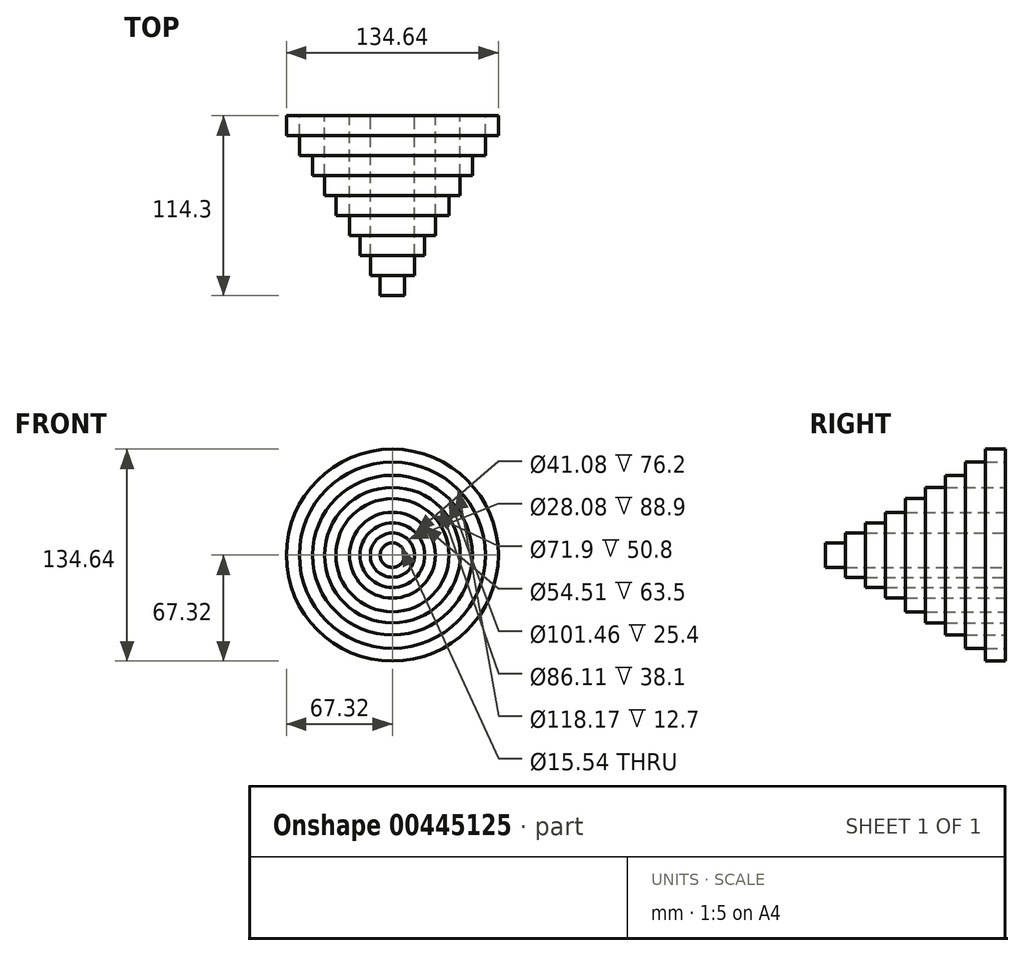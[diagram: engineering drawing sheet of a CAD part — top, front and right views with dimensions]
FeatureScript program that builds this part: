
annotation { "Feature Type Name" : "Feature", "Feature Type Description" : "" }
export const myFeature = defineFeature(function(context is Context, id is Id, definition is map)
    precondition{}
    {
        {
            var Q0;
            Q0=qCreatedBy(makeId("Front.planeOp"),FACE);
            var sketch = newSketch(context, id + "F0", { "sketchPlane" : qUnion([Q0])});
            skCircle(sketch, "E0", {"center": v(0, 0) * mm, "radius": 7.77 * mm});
            skCircle(sketch, "E1", {"center": v(0, 0) * mm, "radius": 14.04 * mm});
            skCircle(sketch, "E2", {"center": v(0, 0) * mm, "radius": 20.54 * mm});
            skCircle(sketch, "E3", {"center": v(0, 0) * mm, "radius": 27.26 * mm});
            skCircle(sketch, "E4", {"center": v(0, 0) * mm, "radius": 35.95 * mm});
            skCircle(sketch, "E5", {"center": v(0, 0) * mm, "radius": 43.06 * mm});
            skCircle(sketch, "E6", {"center": v(0, 0) * mm, "radius": 50.73 * mm});
            skCircle(sketch, "E7", {"center": v(0, 0) * mm, "radius": 59.08 * mm});
            skCircle(sketch, "E8", {"center": v(0, 0) * mm, "radius": 67.32 * mm});
            skSolve(sketch);
        }
        {
            var Q0;
            Q0 = qSketchRegion(id + "F0", true);
            extrude(context, id + "F1", {"entities" : qUnion([Q0]), "depth" : 12.7 * mm});
        }
        {
            var Q0;
            Q0=makeQuery(id+"F0.imprint","IMPRINT",FACE,{"disambiguationData":[TD([[makeQuery(id+"F0.imprint","IMPRINT",EDGE,{"derivedFrom":sQuery(id+"F0.wireOp",EDGE,"E6")}),-1.0]])]});
            extrude(context, id + "F2", {"entities" : qUnion([Q0]), "depth" : 25.4 * mm});
        }
        {
            var Q0;
            Q0=makeQuery(id+"F0.imprint","IMPRINT",FACE,{"disambiguationData":[TD([[makeQuery(id+"F0.imprint","IMPRINT",EDGE,{"derivedFrom":sQuery(id+"F0.wireOp",EDGE,"E5")}),-1.0]])]});
            extrude(context, id + "F3", {"entities" : qUnion([Q0]), "depth" : 38.1 * mm});
        }
        {
            var Q0;
            Q0=makeQuery(id+"F0.imprint","IMPRINT",FACE,{"disambiguationData":[TD([[makeQuery(id+"F0.imprint","IMPRINT",EDGE,{"derivedFrom":sQuery(id+"F0.wireOp",EDGE,"E4")}),-1.0]])]});
            extrude(context, id + "F4", {"entities" : qUnion([Q0]), "depth" : 50.8 * mm});
        }
        {
            var Q0;
            Q0=makeQuery(id+"F0.imprint","IMPRINT",FACE,{"disambiguationData":[TD([[makeQuery(id+"F0.imprint","IMPRINT",EDGE,{"derivedFrom":sQuery(id+"F0.wireOp",EDGE,"E3")}),-1.0]])]});
            extrude(context, id + "F5", {"entities" : qUnion([Q0]), "depth" : 63.5 * mm});
        }
        {
            var Q0;
            Q0=makeQuery(id+"F0.imprint","IMPRINT",FACE,{"disambiguationData":[TD([[makeQuery(id+"F0.imprint","IMPRINT",EDGE,{"derivedFrom":sQuery(id+"F0.wireOp",EDGE,"E2")}),-1.0]])]});
            extrude(context, id + "F6", {"entities" : qUnion([Q0]), "depth" : 76.2 * mm});
        }
        {
            var Q0;
            Q0=makeQuery(id+"F0.imprint","IMPRINT",FACE,{"disambiguationData":[TD([[makeQuery(id+"F0.imprint","IMPRINT",EDGE,{"derivedFrom":sQuery(id+"F0.wireOp",EDGE,"E1")}),-1.0]])]});
            extrude(context, id + "F7", {"entities" : qUnion([Q0]), "depth" : 88.9 * mm});
        }
        {
            var Q0;
            Q0=makeQuery(id+"F0.imprint","IMPRINT",FACE,{"disambiguationData":[TD([[makeQuery(id+"F0.imprint","IMPRINT",EDGE,{"derivedFrom":sQuery(id+"F0.wireOp",EDGE,"E0")}),-1.0]])]});
            extrude(context, id + "F8", {"entities" : qUnion([Q0]), "depth" : 101.6 * mm});
        }
        {
            var Q0;
            Q0=makeQuery(id+"F0.imprint","IMPRINT",FACE,{"disambiguationData":[TD([[makeQuery(id+"F0.imprint","IMPRINT",EDGE,{"derivedFrom":sQuery(id+"F0.wireOp",EDGE,"E0")}),1.0]])]});
            extrude(context, id + "F9", {"entities" : qUnion([Q0]), "depth" : 114.3 * mm});
        }
    });
